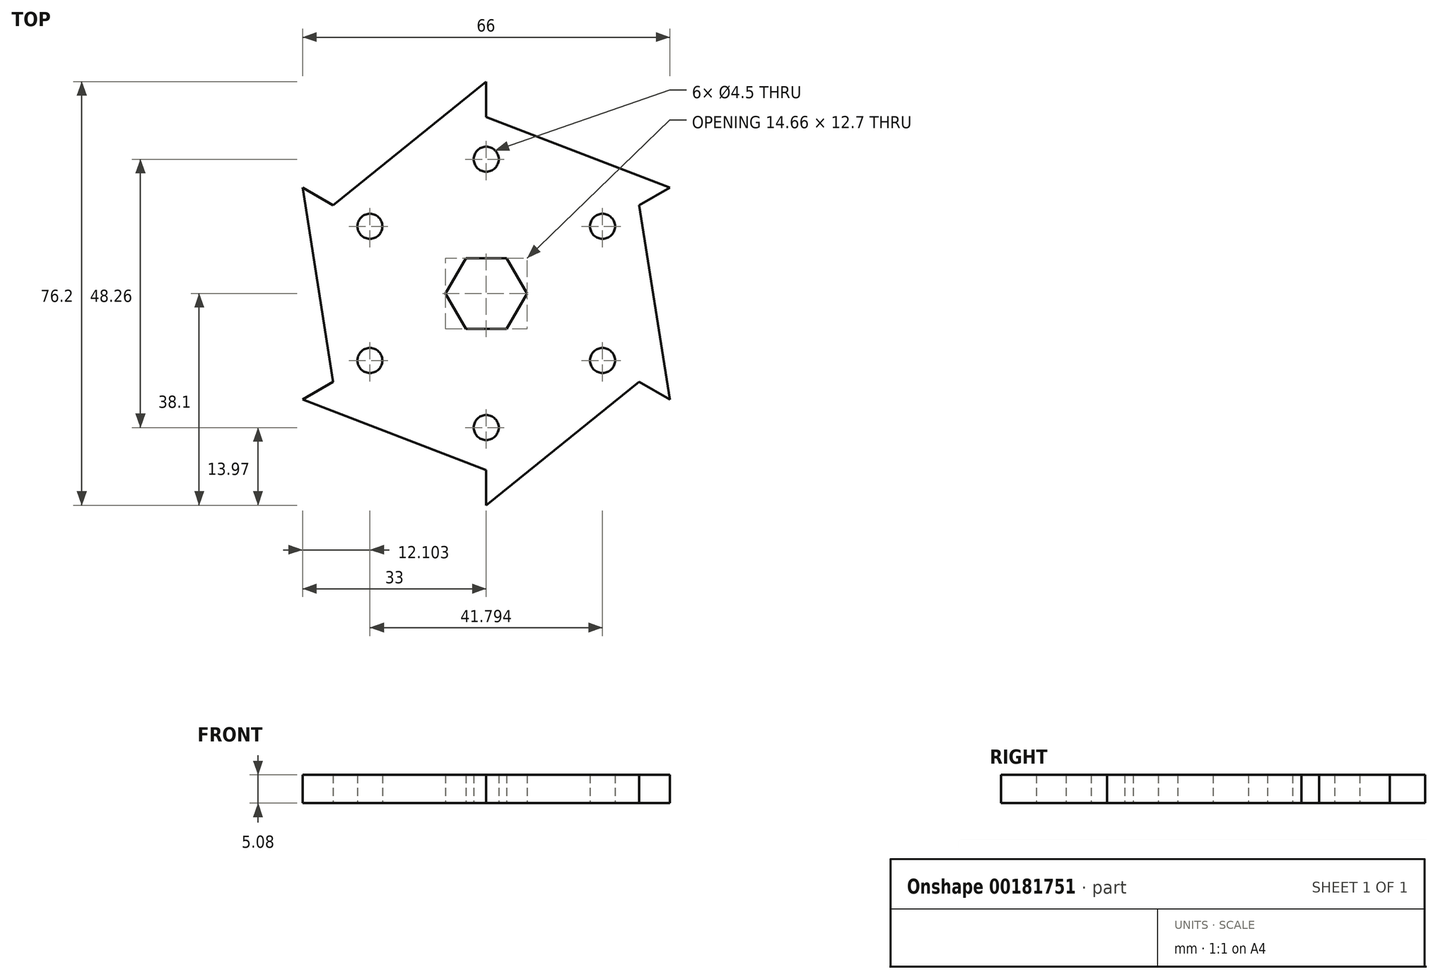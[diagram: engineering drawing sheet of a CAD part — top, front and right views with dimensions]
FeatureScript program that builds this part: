
annotation { "Feature Type Name" : "Feature", "Feature Type Description" : "" }
export const myFeature = defineFeature(function(context is Context, id is Id, definition is map)
    precondition{}
    {
        {
            var Q0;
            Q0=qCreatedBy(makeId("Top.planeOp"),FACE);
            var sketch = newSketch(context, id + "F0", { "sketchPlane" : qUnion([Q0])});
            skCircle(sketch, "E0", {"center": v(0, 0) * mm, "radius": 31.75 * mm, "construction": true});
            skCircle(sketch, "E1", {"center": v(0, 0) * mm, "radius": 38.1 * mm, "construction": true});
            skCircle(sketch, "E2.cCircle", {"center": v(0, 0) * mm, "radius": 6.35 * mm, "construction": true});
            skLineSegment(sketch, "E2.0", {"start": v(-3.67, 6.35) * mm, "end": v(3.67, 6.35) * mm});
            skLineSegment(sketch, "E2.1", {"start": v(3.67, 6.35) * mm, "end": v(7.33, 0) * mm});
            skLineSegment(sketch, "E2.2", {"start": v(7.33, 0) * mm, "end": v(3.67, -6.35) * mm});
            skLineSegment(sketch, "E2.3", {"start": v(3.67, -6.35) * mm, "end": v(-3.67, -6.35) * mm});
            skLineSegment(sketch, "E2.4", {"start": v(-3.67, -6.35) * mm, "end": v(-7.33, 0) * mm});
            skLineSegment(sketch, "E2.5", {"start": v(-7.33, 0) * mm, "end": v(-3.67, 6.35) * mm});
            skPoint(sketch, "E2.0.midPoint", {"position": v(0, 6.35) * mm});
            skCircle(sketch, "E3", {"center": v(0, 24.13) * mm, "radius": 2.25 * mm});
            skCircle(sketch, "E4.1.0", {"center": v(-20.9, 12.07) * mm, "radius": 2.25 * mm});
            skCircle(sketch, "E4.2.0", {"center": v(-20.9, -12.06) * mm, "radius": 2.25 * mm});
            skCircle(sketch, "E4.3.0", {"center": v(0, -24.13) * mm, "radius": 2.25 * mm});
            skCircle(sketch, "E4.4.0", {"center": v(20.9, -12.07) * mm, "radius": 2.25 * mm});
            skCircle(sketch, "E4.5.0", {"center": v(20.9, 12.07) * mm, "radius": 2.25 * mm});
            skCircle(sketch, "E5", {"center": v(0, 0) * mm, "radius": 24.13 * mm, "construction": true});
            skLineSegment(sketch, "E6", {"start": v(0, 0) * mm, "end": v(33, 19.05) * mm, "construction": true});
            skLineSegment(sketch, "E7", {"start": v(0, 38.1) * mm, "end": v(0, 31.75) * mm});
            skLineSegment(sketch, "E8", {"start": v(0, 31.75) * mm, "end": v(33, 19.05) * mm});
            skLineSegment(sketch, "E9.1.0", {"start": v(-27.5, 15.88) * mm, "end": v(0, 38.1) * mm});
            skLineSegment(sketch, "E9.1.1", {"start": v(-33, 19.05) * mm, "end": v(-27.5, 15.88) * mm});
            skLineSegment(sketch, "E9.2.0", {"start": v(-27.5, -15.87) * mm, "end": v(-33, 19.05) * mm});
            skLineSegment(sketch, "E9.2.1", {"start": v(-33, -19.05) * mm, "end": v(-27.5, -15.87) * mm});
            skLineSegment(sketch, "E9.3.0", {"start": v(0, -31.75) * mm, "end": v(-33, -19.05) * mm});
            skLineSegment(sketch, "E9.3.1", {"start": v(0, -38.1) * mm, "end": v(0, -31.75) * mm});
            skLineSegment(sketch, "E9.4.0", {"start": v(27.5, -15.88) * mm, "end": v(0, -38.1) * mm});
            skLineSegment(sketch, "E9.4.1", {"start": v(33, -19.05) * mm, "end": v(27.5, -15.88) * mm});
            skLineSegment(sketch, "E9.5.0", {"start": v(27.5, 15.88) * mm, "end": v(33, -19.05) * mm});
            skLineSegment(sketch, "E9.5.1", {"start": v(33, 19.05) * mm, "end": v(27.5, 15.88) * mm});
            skLineSegment(sketch, "E10", {"start": v(0, 38.1) * mm, "end": v(0, 0) * mm, "construction": true});
            skSolve(sketch);
        }
        {
            var Q0;
            Q0=makeQuery(id+"F0.imprint","IMPRINT",FACE,{"disambiguationData":[TD([[makeQuery(id+"F0.imprint","IMPRINT",EDGE,{"derivedFrom":sQuery(id+"F0.wireOp",EDGE,"E2.0")}),1.0]])]});
            extrude(context, id + "F1", {"entities" : qUnion([Q0]), "depth" : 5.08 * mm});
        }
    });
